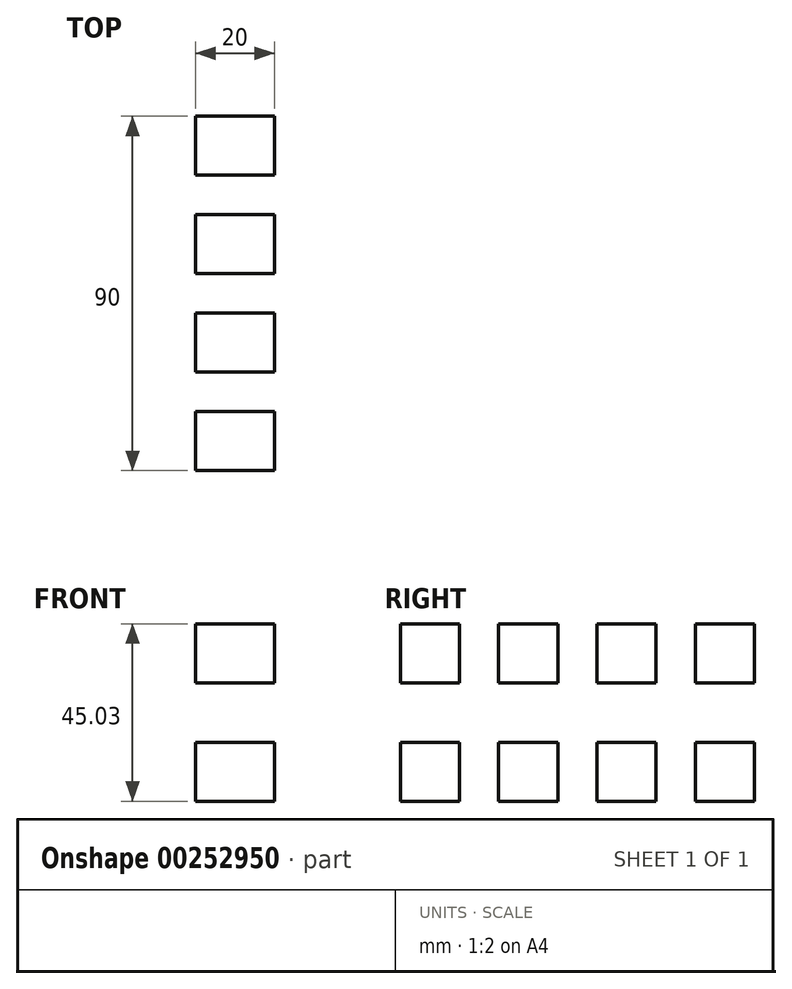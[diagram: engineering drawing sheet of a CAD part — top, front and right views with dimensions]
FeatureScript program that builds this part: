
annotation { "Feature Type Name" : "Feature", "Feature Type Description" : "" }
export const myFeature = defineFeature(function(context is Context, id is Id, definition is map)
    precondition{}
    {
        {
            var Q0;
            Q0=qCreatedBy(makeId("Right.planeOp"),FACE);
            var sketch = newSketch(context, id + "F0", { "sketchPlane" : qUnion([Q0])});
            skLineSegment(sketch, "E0.bottom", {"start": v(-61.74, 47.58) * mm, "end": v(-46.74, 47.58) * mm});
            skLineSegment(sketch, "E0.top", {"start": v(-61.74, 32.58) * mm, "end": v(-46.74, 32.58) * mm});
            skLineSegment(sketch, "E0.left", {"start": v(-61.74, 47.58) * mm, "end": v(-61.74, 32.58) * mm});
            skLineSegment(sketch, "E0.right", {"start": v(-46.74, 47.58) * mm, "end": v(-46.74, 32.58) * mm});
            skLineSegment(sketch, "E1.bottom", {"start": v(-36.74, 47.58) * mm, "end": v(-21.74, 47.58) * mm});
            skLineSegment(sketch, "E1.top", {"start": v(-36.74, 32.58) * mm, "end": v(-21.74, 32.58) * mm});
            skLineSegment(sketch, "E1.left", {"start": v(-36.74, 47.58) * mm, "end": v(-36.74, 32.58) * mm});
            skLineSegment(sketch, "E1.right", {"start": v(-21.74, 47.58) * mm, "end": v(-21.74, 32.58) * mm});
            skLineSegment(sketch, "E2.bottom", {"start": v(-11.74, 47.58) * mm, "end": v(3.26, 47.58) * mm});
            skLineSegment(sketch, "E2.top", {"start": v(-11.74, 32.58) * mm, "end": v(3.26, 32.58) * mm});
            skLineSegment(sketch, "E2.left", {"start": v(-11.74, 47.58) * mm, "end": v(-11.74, 32.58) * mm});
            skLineSegment(sketch, "E2.right", {"start": v(3.26, 47.58) * mm, "end": v(3.26, 32.58) * mm});
            skLineSegment(sketch, "E3.bottom", {"start": v(13.26, 47.58) * mm, "end": v(28.26, 47.58) * mm});
            skLineSegment(sketch, "E3.top", {"start": v(13.26, 32.58) * mm, "end": v(28.26, 32.58) * mm});
            skLineSegment(sketch, "E3.left", {"start": v(13.26, 47.58) * mm, "end": v(13.26, 32.58) * mm});
            skLineSegment(sketch, "E3.right", {"start": v(28.26, 47.58) * mm, "end": v(28.26, 32.58) * mm});
            skLineSegment(sketch, "E4.bottom", {"start": v(-61.74, 17.55) * mm, "end": v(-46.74, 17.55) * mm});
            skLineSegment(sketch, "E4.top", {"start": v(-61.74, 2.55) * mm, "end": v(-46.74, 2.55) * mm});
            skLineSegment(sketch, "E4.left", {"start": v(-61.74, 17.55) * mm, "end": v(-61.74, 2.55) * mm});
            skLineSegment(sketch, "E4.right", {"start": v(-46.74, 17.55) * mm, "end": v(-46.74, 2.55) * mm});
            skLineSegment(sketch, "E5.bottom", {"start": v(-36.74, 17.55) * mm, "end": v(-21.74, 17.55) * mm});
            skLineSegment(sketch, "E5.top", {"start": v(-36.74, 2.55) * mm, "end": v(-21.74, 2.55) * mm});
            skLineSegment(sketch, "E5.left", {"start": v(-36.74, 17.55) * mm, "end": v(-36.74, 2.55) * mm});
            skLineSegment(sketch, "E5.right", {"start": v(-21.74, 17.55) * mm, "end": v(-21.74, 2.55) * mm});
            skLineSegment(sketch, "E6.bottom", {"start": v(-11.74, 17.55) * mm, "end": v(3.26, 17.55) * mm});
            skLineSegment(sketch, "E6.top", {"start": v(-11.74, 2.55) * mm, "end": v(3.26, 2.55) * mm});
            skLineSegment(sketch, "E6.left", {"start": v(-11.74, 17.55) * mm, "end": v(-11.74, 2.55) * mm});
            skLineSegment(sketch, "E6.right", {"start": v(3.26, 17.55) * mm, "end": v(3.26, 2.55) * mm});
            skLineSegment(sketch, "E7.bottom", {"start": v(13.26, 17.55) * mm, "end": v(28.26, 17.55) * mm});
            skLineSegment(sketch, "E7.top", {"start": v(13.26, 2.55) * mm, "end": v(28.26, 2.55) * mm});
            skLineSegment(sketch, "E7.left", {"start": v(13.26, 17.55) * mm, "end": v(13.26, 2.55) * mm});
            skLineSegment(sketch, "E7.right", {"start": v(28.26, 17.55) * mm, "end": v(28.26, 2.55) * mm});
            skSolve(sketch);
        }
        {
            var Q0;
            Q0 = qSketchRegion(id + "F0", true);
            extrude(context, id + "F1", {"entities" : qUnion([Q0]), "depth" : 20 * mm});
        }
    });
